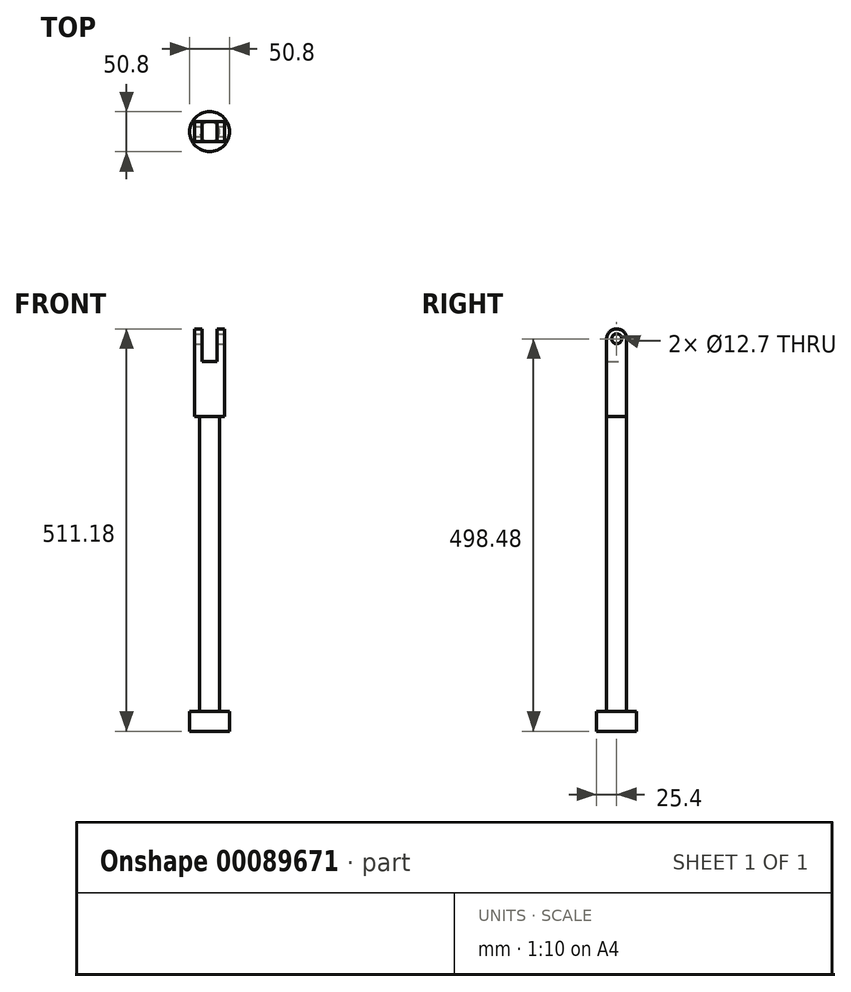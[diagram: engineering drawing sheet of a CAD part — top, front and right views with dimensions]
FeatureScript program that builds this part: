
annotation { "Feature Type Name" : "Feature", "Feature Type Description" : "" }
export const myFeature = defineFeature(function(context is Context, id is Id, definition is map)
    precondition{}
    {
        {
            var Q0;
            Q0=qCreatedBy(makeId("Top.planeOp"),FACE);
            var sketch = newSketch(context, id + "F0", { "sketchPlane" : qUnion([Q0])});
            skCircle(sketch, "E0", {"center": v(0, 0) * mm, "radius": 12.7 * mm});
            skSolve(sketch);
        }
        {
            var Q0;
            Q0 = qSketchRegion(id + "F0", true);
            extrude(context, id + "F1", {"entities" : qUnion([Q0]), "endBound" : BoundingType.SYMMETRIC, "depth" : 374.65 * mm});
        }
        {
            var Q0;
            Q0=makeQuery(id+"F1.opExtrude","CAP_FACE",FACE,{"disambiguationData":[OSD([sQuery(id+"F0.wireOp",EDGE,"E0")])],"isStart":false});
            cPlane(context, id + "F2", {"entities" : qUnion([Q0]), "cplaneType" : CPlaneType.OFFSET, "offset" : 0 * mm, "width" : 152.4 * mm, "height" : 152.4 * mm});
        }
        {
            var Q0;
            Q0=qCreatedBy(id+"F2.planeOp",FACE);
            var sketch = newSketch(context, id + "F3", { "sketchPlane" : qUnion([Q0])});
            skLineSegment(sketch, "E1.bottom", {"start": v(-19.05, 12.7) * mm, "end": v(19.05, 12.7) * mm});
            skLineSegment(sketch, "E1.top", {"start": v(-19.05, -12.7) * mm, "end": v(19.05, -12.7) * mm});
            skLineSegment(sketch, "E1.left", {"start": v(-19.05, 12.7) * mm, "end": v(-19.05, -12.7) * mm});
            skLineSegment(sketch, "E1.right", {"start": v(19.05, 12.7) * mm, "end": v(19.05, -12.7) * mm});
            skPoint(sketch, "E1.middle", {"position": v(0, 0) * mm});
            skSolve(sketch);
        }
        {
            var Q0;
            Q0 = qSketchRegion(id + "F3", true);
            extrude(context, id + "F4", {"entities" : qUnion([Q0]), "operationType" : NewBodyOperationType.ADD, "depth" : 98.42 * mm});
        }
        {
            var Q0;
            Q0=makeQuery(id+"F4.opExtrude","CAP_FACE",FACE,{"disambiguationData":[OSD([sQuery(id+"F3.wireOp",EDGE,"E1.bottom"),sQuery(id+"F3.wireOp",EDGE,"E1.top"),sQuery(id+"F3.wireOp",EDGE,"E1.left"),sQuery(id+"F3.wireOp",EDGE,"E1.right")])],"isStart":false});
            var sketch = newSketch(context, id + "F5", { "sketchPlane" : qUnion([Q0])});
            skLineSegment(sketch, "E2.bottom", {"start": v(-19.05, 12.7) * mm, "end": v(19.05, 12.7) * mm});
            skLineSegment(sketch, "E2.top", {"start": v(-19.05, 0) * mm, "end": v(19.05, 0) * mm});
            skLineSegment(sketch, "E2.left", {"start": v(-19.05, 12.7) * mm, "end": v(-19.05, 0) * mm});
            skLineSegment(sketch, "E2.right", {"start": v(19.05, 12.7) * mm, "end": v(19.05, 0) * mm});
            skSolve(sketch);
        }
        {
            var Q0;
            Q0 = qSketchRegion(id + "F5", true);
            var Q1;
            Q1=sQuery(id+"F5.wireOp",EDGE,"E2.top");
            revolve(context, id + "F6", {"operationType" : NewBodyOperationType.ADD, "entities" : qUnion([Q0]), "axis" : qUnion([Q1]), "revolveType" : RevolveType.FULL});
        }
        {
            var Q0;
            Q0=makeQuery(id+"F6.boolean.opBoolean","MERGE",FACE,{"derivedFrom":[makeQuery(id+"F4.opExtrude","SWEPT_FACE",FACE,{"disambiguationData":[OSD([sQuery(id+"F3.wireOp",EDGE,"E1.right")])]}),makeQuery(id+"F6.opRevolve","SWEPT_FACE",FACE,{"disambiguationData":[OSD([sQuery(id+"F5.wireOp",EDGE,"E2.right")])]})]});
            var sketch = newSketch(context, id + "F7", { "sketchPlane" : qUnion([Q0])});
            skPoint(sketch, "E3", {"position": v(0, 285.75) * mm});
            skSolve(sketch);
        }
        {
            var Q0;
            Q0=sQuery(id+"F7.wireOp",VERTEX,"E3");
            var Q1;
            Q1=makeQuery(id+"F1.opExtrude","SWEPT_BODY",BODY,{"disambiguationData":[OSD([sQuery(id+"F0.wireOp",EDGE,"E0")])]});
            hole(context, id + "F8", {"style" : HoleStyle.SIMPLE, "endStyle" : HoleEndStyle.THROUGH, "holeDiameter" : 12.7 * mm, "locations" : qUnion([Q0]), "scope" : qUnion([Q1]), "isTappedThrough" : true});
        }
        {
            var Q0;
            Q0=makeQuery(id+"F1.opExtrude","CAP_FACE",FACE,{"disambiguationData":[OSD([sQuery(id+"F0.wireOp",EDGE,"E0")])],"isStart":true});
            var sketch = newSketch(context, id + "F9", { "sketchPlane" : qUnion([Q0])});
            skCircle(sketch, "E4", {"center": v(0, 0) * mm, "radius": 25.4 * mm});
            skSolve(sketch);
        }
        {
            var Q0;
            Q0 = qSketchRegion(id + "F9", true);
            extrude(context, id + "F10", {"entities" : qUnion([Q0]), "operationType" : NewBodyOperationType.ADD, "depth" : 25.4 * mm});
        }
        {
            var Q0;
            Q0=qCreatedBy(makeId("Right.planeOp"),FACE);
            var sketch = newSketch(context, id + "F11", { "sketchPlane" : qUnion([Q0])});
            skLineSegment(sketch, "E5.bottom", {"start": v(-55.79, 257.18) * mm, "end": v(70, 257.18) * mm});
            skLineSegment(sketch, "E5.top", {"start": v(-55.79, 305.25) * mm, "end": v(70, 305.25) * mm});
            skLineSegment(sketch, "E5.left", {"start": v(-55.79, 257.18) * mm, "end": v(-55.79, 305.25) * mm});
            skLineSegment(sketch, "E5.right", {"start": v(70, 257.18) * mm, "end": v(70, 305.25) * mm});
            skSolve(sketch);
        }
        {
            var Q0;
            Q0=makeQuery(id+"F11.imprint","IMPRINT",FACE,{"disambiguationData":[TD([[makeQuery(id+"F11.imprint","IMPRINT",EDGE,{"derivedFrom":sQuery(id+"F11.wireOp",EDGE,"E5.bottom")}),1.0]])]});
            extrude(context, id + "F12", {"entities" : qUnion([Q0]), "operationType" : NewBodyOperationType.REMOVE, "endBound" : BoundingType.SYMMETRIC, "depth" : 19.05 * mm});
        }
    });
